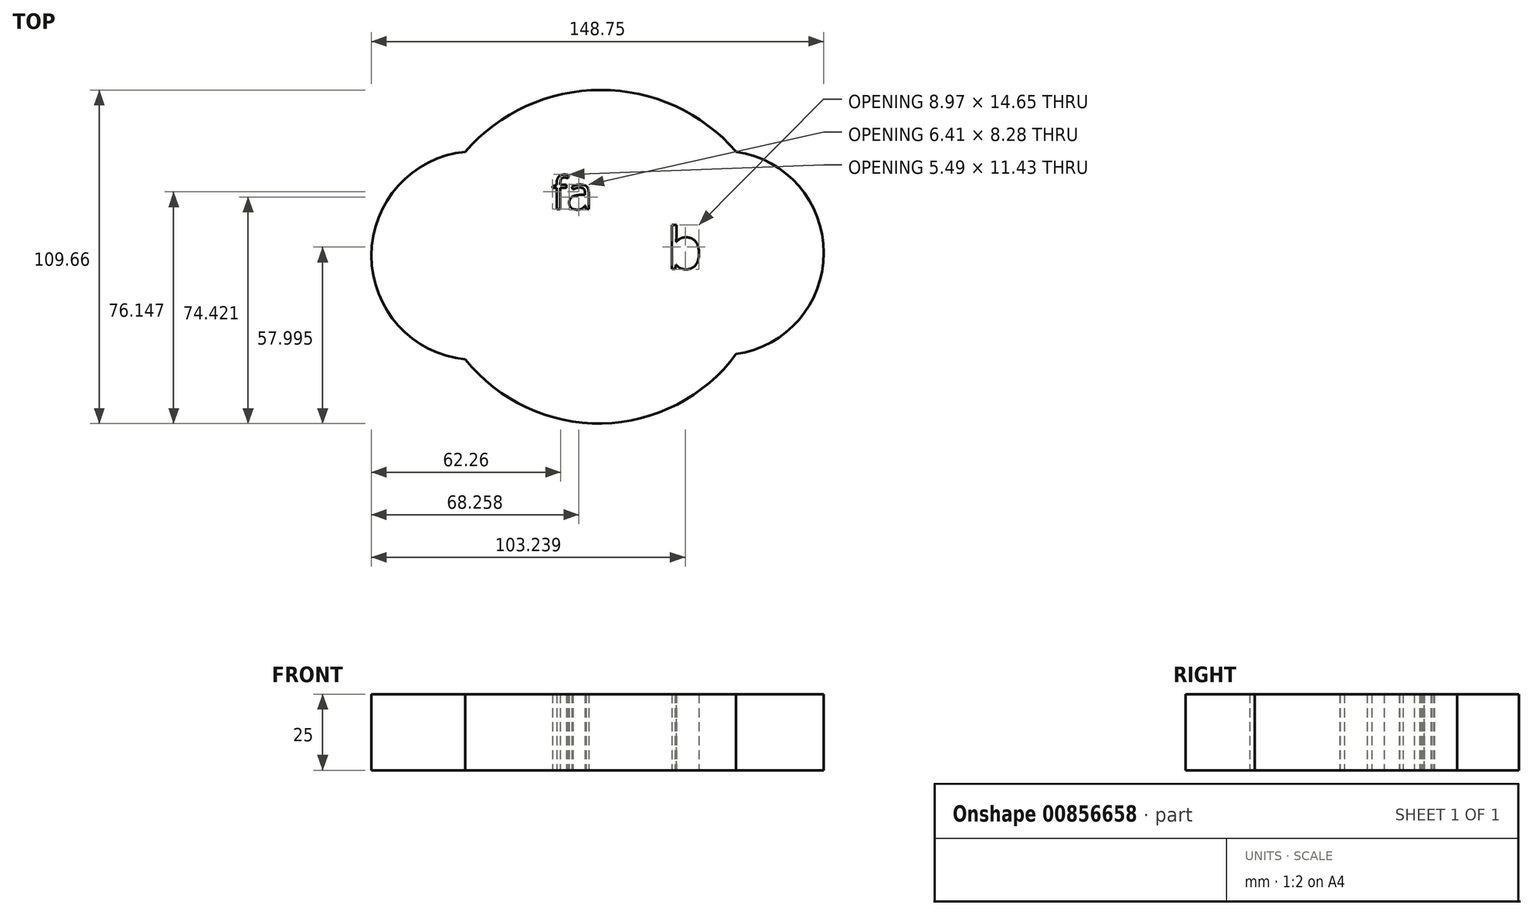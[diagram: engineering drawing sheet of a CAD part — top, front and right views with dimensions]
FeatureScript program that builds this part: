
annotation { "Feature Type Name" : "Feature", "Feature Type Description" : "" }
export const myFeature = defineFeature(function(context is Context, id is Id, definition is map)
    precondition{}
    {
        {
            var Q0;
            Q0=qCreatedBy(makeId("Top.planeOp"),FACE);
            var sketch = newSketch(context, id + "F0", { "sketchPlane" : qUnion([Q0])});
            skLineSegment(sketch, "E0", {"start": v(0, 0) * mm, "end": v(-43.53, 34.9) * mm});
            skLineSegment(sketch, "E1", {"start": v(0, 0) * mm, "end": v(45.49, 34.9) * mm});
            skLineSegment(sketch, "E2", {"start": v(0, 0) * mm, "end": v(45.49, -31.63) * mm});
            skLineSegment(sketch, "E3", {"start": v(0, 0) * mm, "end": v(-43.53, -33.4) * mm});
            skLineSegment(sketch, "E4", {"start": v(-43.53, -33.4) * mm, "end": v(-43.53, 34.9) * mm});
            skLineSegment(sketch, "E5", {"start": v(-43.53, 34.9) * mm, "end": v(45.49, 34.9) * mm});
            skLineSegment(sketch, "E6", {"start": v(45.49, -31.63) * mm, "end": v(45.49, 34.9) * mm});
            skLineSegment(sketch, "E7", {"start": v(45.49, -31.63) * mm, "end": v(-43.53, -33.4) * mm});
            skText(sketch, "E8", { "text": "fa", "fontName": "OpenSans-Regular.ttf"});
            skText(sketch, "E9", { "text": "b", "fontName": "OpenSans-Regular.ttf"});
            skArc(sketch, "E10", {"start": v(45.49, 34.9) * mm, "mid": v(0.98, 55.21) * mm, "end": v(-43.53, 34.9) * mm});
            skArc(sketch, "E11", {"start": v(45.49, -31.63) * mm, "mid": v(74.3, 1.63) * mm, "end": v(45.49, 34.9) * mm});
            skArc(sketch, "E12", {"start": v(-43.53, -33.4) * mm, "mid": v(1.41, -54.44) * mm, "end": v(45.49, -31.63) * mm});
            skArc(sketch, "E13", {"start": v(-43.53, 34.9) * mm, "mid": v(-74.46, 0.75) * mm, "end": v(-43.53, -33.4) * mm});
            const initialGuessF0  = {"E8": [-0.01516, 0.01598, 1, 0, 0.01076], "E9": [0.02266, -0.00359, 1, 0, 0.0137]};
            skSetInitialGuess(sketch, initialGuessF0);
            skSolve(sketch);
        }
        {
            var Q0;
            Q0 = qSketchRegion(id + "F0", true);
            extrude(context, id + "F1", {"entities" : qUnion([Q0]), "depth" : 25 * mm, "offsetDistance" : 25 * mm});
        }
    });
